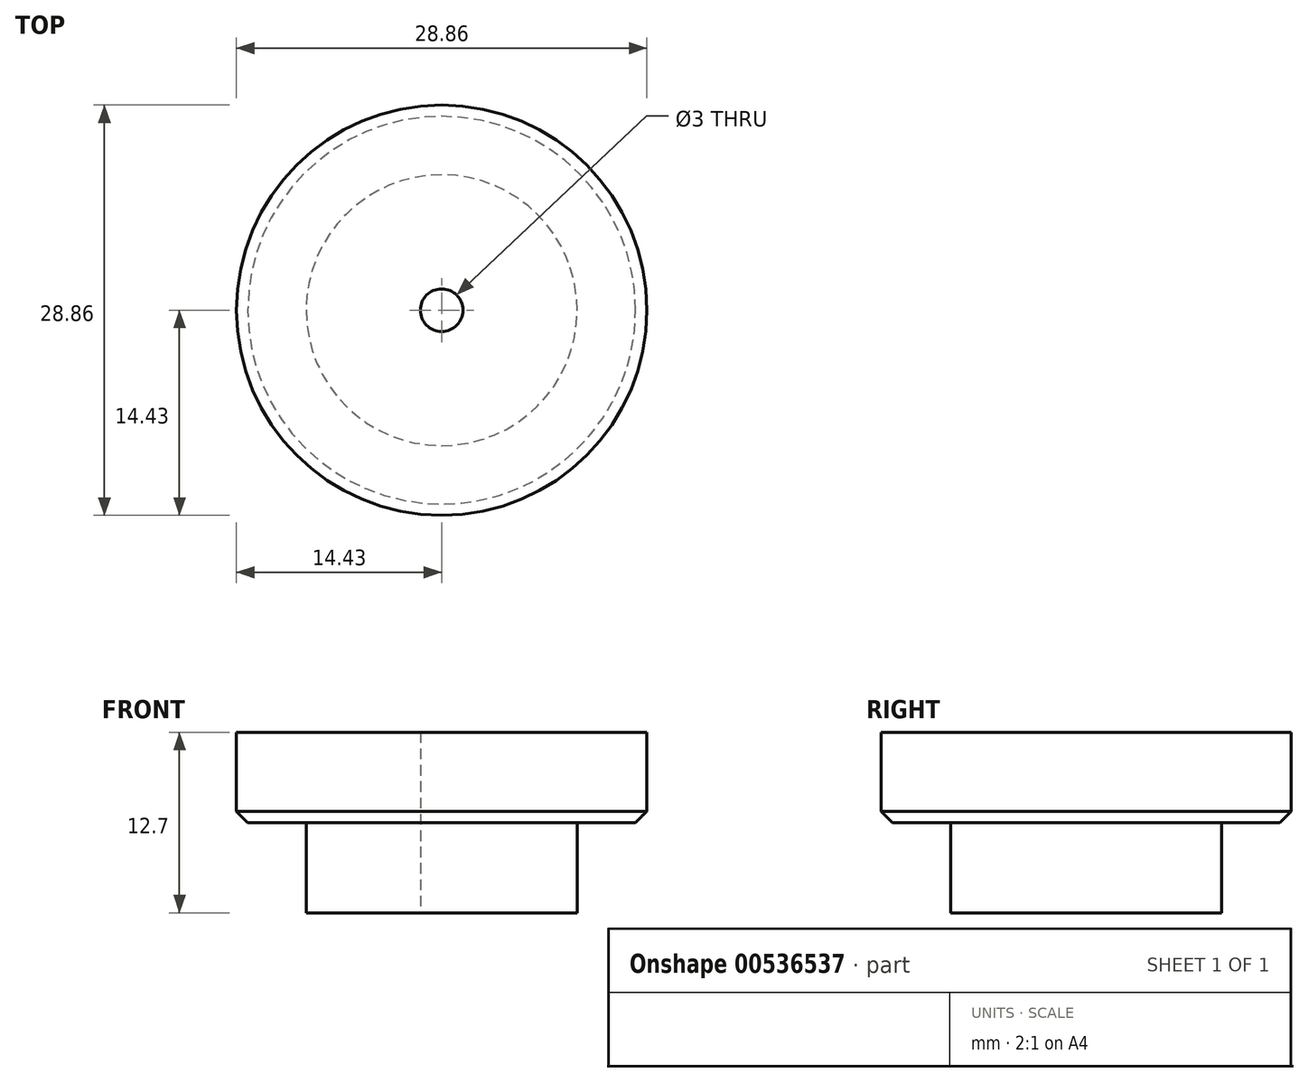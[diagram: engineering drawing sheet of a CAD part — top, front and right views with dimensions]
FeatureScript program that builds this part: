
annotation { "Feature Type Name" : "Feature", "Feature Type Description" : "" }
export const myFeature = defineFeature(function(context is Context, id is Id, definition is map)
    precondition{}
    {
        {
            var Q0;
            Q0=qCreatedBy(makeId("Front.planeOp"),FACE);
            var sketch = newSketch(context, id + "F0", { "sketchPlane" : qUnion([Q0])});
            skLineSegment(sketch, "E0", {"start": v(0, 0) * mm, "end": v(14.43, 0) * mm});
            skLineSegment(sketch, "E1", {"start": v(14.43, 0) * mm, "end": v(14.43, -6.35) * mm});
            skLineSegment(sketch, "E2", {"start": v(14.43, -6.35) * mm, "end": v(9.52, -6.35) * mm});
            skLineSegment(sketch, "E3", {"start": v(9.53, -6.35) * mm, "end": v(9.53, -12.7) * mm});
            skLineSegment(sketch, "E4", {"start": v(9.52, -12.7) * mm, "end": v(0, -12.7) * mm});
            skLineSegment(sketch, "E5", {"start": v(0, -12.7) * mm, "end": v(0, 0) * mm});
            skSolve(sketch);
        }
        {
            var Q0;
            Q0=qSketchRegion(id+"F0",true);
            var Q1;
            Q1=sQuery(id+"F0.wireOp",EDGE,"E5");
            revolve(context, id + "F1", {"entities" : qUnion([Q0]), "axis" : qUnion([Q1]), "revolveType" : RevolveType.FULL});
        }
        {
            var Q0;
            Q0=makeQuery(id+"F1.opRevolve","SWEPT_FACE",FACE,{"disambiguationData":[OSD([sQuery(id+"F0.wireOp",EDGE,"E0")])]});
            var sketch = newSketch(context, id + "F2", { "sketchPlane" : qUnion([Q0])});
            skPoint(sketch, "E6", {"position": v(0, 0) * mm});
            skSolve(sketch);
        }
        {
            var Q0;
            Q0=sQuery(id+"F2.wireOp",VERTEX,"E6");
            var Q1;
            Q1=makeQuery(id+"F1.opRevolve","SWEPT_BODY",BODY,{"disambiguationData":[OSD([sQuery(id+"F0.wireOp",EDGE,"E0"),sQuery(id+"F0.wireOp",EDGE,"E1"),sQuery(id+"F0.wireOp",EDGE,"uxOOcbma-rM4K-7eKG-5Tp7-zW7kDo2e6Tqz"),sQuery(id+"F0.wireOp",EDGE,"NVDGhDdD-NORQ-odFN-u7FE-xEci0S9tA2uR"),sQuery(id+"F0.wireOp",EDGE,"E2"),sQuery(id+"F0.wireOp",EDGE,"E3"),sQuery(id+"F0.wireOp",EDGE,"E4"),sQuery(id+"F0.wireOp",EDGE,"E5")])]});
            hole(context, id + "F3", {"style" : HoleStyle.SIMPLE, "endStyle" : HoleEndStyle.THROUGH, "standardTappedOrClearance" : lookupTablePath({ "standard" : "ANSI", "size" : "#46 (0.08)", "type" : "Drilled" }), "standardBlindInLast" : lookupTablePath({ "standard" : "ANSI", "size" : "#46", "type" : "Drilled" }), "holeDiameter" : 2.06 * mm, "tappedDepth" : 25.4 * mm, "tapClearance" : 3, "startFromSketch" : true, "locations" : qUnion([Q0]), "scope" : qUnion([Q1])});
        }
        {
            var Q0;
            Q0=makeQuery(id+"F1.opRevolve","SWEPT_FACE",FACE,{"disambiguationData":[OSD([sQuery(id+"F0.wireOp",EDGE,"E4")])]});
            var sketch = newSketch(context, id + "F4", { "sketchPlane" : qUnion([Q0])});
            skPoint(sketch, "E7", {"position": v(0, 0) * mm});
            skSolve(sketch);
        }
        {
            var Q0;
            Q0=sQuery(id+"F4.wireOp",VERTEX,"E7");
            var Q1;
            Q1=makeQuery(id+"F1.opRevolve","SWEPT_BODY",BODY,{"disambiguationData":[OSD([sQuery(id+"F0.wireOp",EDGE,"E0"),sQuery(id+"F0.wireOp",EDGE,"E1"),sQuery(id+"F0.wireOp",EDGE,"uxOOcbma-rM4K-7eKG-5Tp7-zW7kDo2e6Tqz"),sQuery(id+"F0.wireOp",EDGE,"NVDGhDdD-NORQ-odFN-u7FE-xEci0S9tA2uR"),sQuery(id+"F0.wireOp",EDGE,"E2"),sQuery(id+"F0.wireOp",EDGE,"E3"),sQuery(id+"F0.wireOp",EDGE,"E4"),sQuery(id+"F0.wireOp",EDGE,"E5")])]});
            hole(context, id + "F5", {"style" : HoleStyle.SIMPLE, "endStyle" : HoleEndStyle.BLIND, "standardTappedOrClearance" : lookupTablePath({ "standard" : "ISO", "size" : "3", "type" : "Drilled" }), "standardBlindInLast" : lookupTablePath({ "standard" : "ISO", "size" : "3", "type" : "Drilled" }), "holeDiameter" : 3 * mm, "holeDepth" : 19.05 * mm, "tappedDepth" : 25.4 * mm, "tapClearance" : 3, "startFromSketch" : true, "locations" : qUnion([Q0]), "scope" : qUnion([Q1])});
        }
        {
            var Q0;
            Q0=makeQuery(id+"F1.opRevolve","SWEPT_EDGE",EDGE,{"disambiguationData":[OSD([sQuery(id+"F0.wireOp",EDGE,"E1"),sQuery(id+"F0.wireOp",EDGE,"E2")])]});
            chamfer(context, id + "F6", {"entities" : qUnion([Q0]), "width" : 0.8 * mm, "tangentPropagation" : true});
        }
    });
